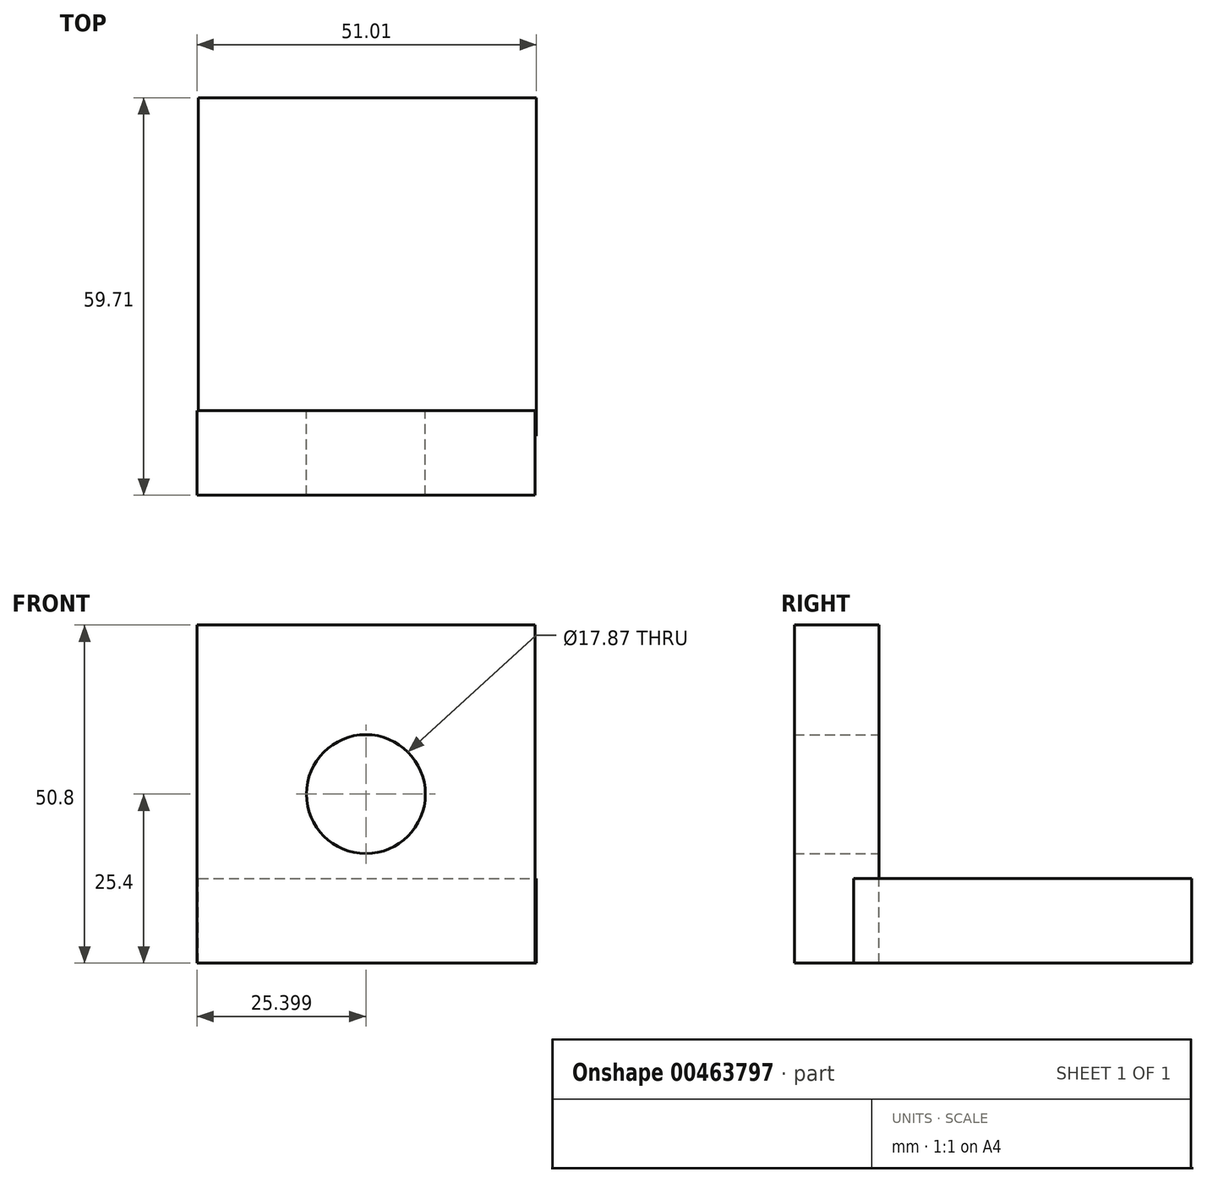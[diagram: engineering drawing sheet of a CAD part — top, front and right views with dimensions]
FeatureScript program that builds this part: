
annotation { "Feature Type Name" : "Feature", "Feature Type Description" : "" }
export const myFeature = defineFeature(function(context is Context, id is Id, definition is map)
    precondition{}
    {
        {
            var Q0;
            Q0=qCreatedBy(makeId("Top.planeOp"),FACE);
            var sketch = newSketch(context, id + "F0", { "sketchPlane" : qUnion([Q0])});
            skLineSegment(sketch, "E0.bottom", {"start": v(-31.05, -3.8) * mm, "end": v(19.75, -3.8) * mm});
            skLineSegment(sketch, "E0.top", {"start": v(-31.05, 47) * mm, "end": v(19.75, 47) * mm});
            skLineSegment(sketch, "E0.left", {"start": v(-31.05, -3.8) * mm, "end": v(-31.05, 47) * mm});
            skLineSegment(sketch, "E0.right", {"start": v(19.75, -3.8) * mm, "end": v(19.75, 47) * mm});
            skSolve(sketch);
        }
        {
            var Q0;
            Q0 = qSketchRegion(id + "F0", true);
            extrude(context, id + "F1", {"entities" : qUnion([Q0]), "depth" : 12.7 * mm});
        }
        {
            var Q0;
            Q0=qCreatedBy(makeId("Front.planeOp"),FACE);
            var sketch = newSketch(context, id + "F2", { "sketchPlane" : qUnion([Q0])});
            skLineSegment(sketch, "E1.bottom", {"start": v(-31.26, 0) * mm, "end": v(19.54, 0) * mm});
            skLineSegment(sketch, "E1.top", {"start": v(-31.26, 50.8) * mm, "end": v(19.54, 50.8) * mm});
            skLineSegment(sketch, "E1.left", {"start": v(-31.26, 0) * mm, "end": v(-31.26, 50.8) * mm});
            skLineSegment(sketch, "E1.right", {"start": v(19.54, 0) * mm, "end": v(19.54, 50.8) * mm});
            skCircle(sketch, "E2", {"center": v(-5.86, 25.4) * mm, "radius": 8.94 * mm});
            skPoint(sketch, "E2.centerSnap0", {"position": v(-5.86, 50.8) * mm});
            skPoint(sketch, "E2.centerSnap1", {"position": v(-31.26, 25.4) * mm});
            skSolve(sketch);
        }
        {
            var Q0;
            Q0 = qSketchRegion(id + "F2", true);
            extrude(context, id + "F3", {"entities" : qUnion([Q0]), "operationType" : NewBodyOperationType.ADD, "depth" : 12.7 * mm});
        }
        {
            var Q0;
            Q0 = qSketchRegion(id + "F2", true);
            extrude(context, id + "F4", {"entities" : qUnion([Q0]), "operationType" : NewBodyOperationType.ADD, "depth" : 12.7 * mm});
        }
    });
